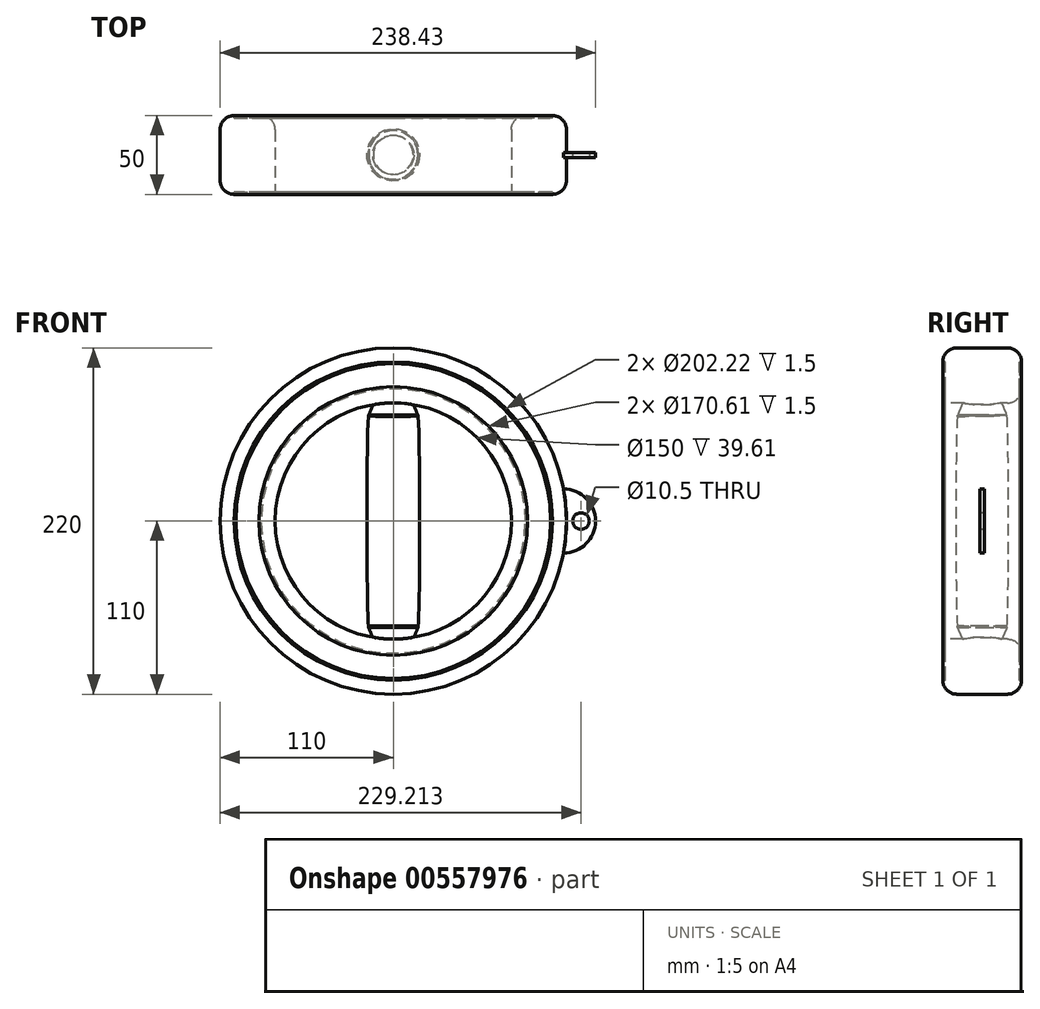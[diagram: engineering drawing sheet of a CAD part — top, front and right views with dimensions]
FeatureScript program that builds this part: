
annotation { "Feature Type Name" : "Feature", "Feature Type Description" : "" }
export const myFeature = defineFeature(function(context is Context, id is Id, definition is map)
    precondition{}
    {
        {
            var Q0;
            Q0=qCreatedBy(makeId("Front.planeOp"),FACE);
            var sketch = newSketch(context, id + "F0", { "sketchPlane" : qUnion([Q0])});
            skCircle(sketch, "E0", {"center": v(0, 0) * mm, "radius": 110 * mm});
            skSolve(sketch);
        }
        {
            var Q0;
            Q0 = qSketchRegion(id + "F0", true);
            extrude(context, id + "F1", {"entities" : qUnion([Q0]), "depth" : 50 * mm, "offsetDistance" : 25.4 * mm});
        }
        {
            var Q0;
            Q0=makeQuery(id+"F1.opExtrude","CAP_FACE",FACE,{"disambiguationData":[OSD([sQuery(id+"F0.wireOp",EDGE,"E0")])],"isStart":false});
            var sketch = newSketch(context, id + "F2", { "sketchPlane" : qUnion([Q0])});
            skCircle(sketch, "E1", {"center": v(0, 0) * mm, "radius": 75 * mm});
            skSolve(sketch);
        }
        {
            var Q0;
            Q0 = qSketchRegion(id + "F2", true);
            extrude(context, id + "F3", {"entities" : qUnion([Q0]), "operationType" : NewBodyOperationType.REMOVE, "endBound" : BoundingType.THROUGH_ALL, "oppositeDirection" : true, "depth" : 25.4 * mm, "offsetDistance" : 25.4 * mm});
        }
        {
            var Q0;
            Q0=qCreatedBy(makeId("Top.planeOp"),FACE);
            cPlane(context, id + "F4", {"entities" : qUnion([Q0]), "cplaneType" : CPlaneType.OFFSET, "offset" : 75.18 * mm, "width" : 152.4 * mm, "height" : 152.4 * mm});
        }
        {
            var Q0;
            Q0=makeQuery(id+"F1.opExtrude","CAP_EDGE",EDGE,{"disambiguationData":[OSD([sQuery(id+"F0.wireOp",EDGE,"E0")])],"isStart":false});
            var Q1;
            Q1=makeQuery(id+"F3.boolean.opBoolean","COPY",EDGE,{"derivedFrom":makeQuery(id+"F3.opExtrude","CAP_EDGE",EDGE,{"disambiguationData":[OSD([sQuery(id+"F2.wireOp",EDGE,"E1")])],"isStart":true})});
            var Q2;
            Q2=makeQuery(id+"F1.opExtrude","CAP_EDGE",EDGE,{"disambiguationData":[OSD([sQuery(id+"F0.wireOp",EDGE,"E0")])],"isStart":true});
            var Q3;
            Q3=makeQuery(id+"F3.boolean.opBoolean","INTERSECT",EDGE,{"derivedFrom":[makeQuery(id+"F1.opExtrude","CAP_FACE",FACE,{"disambiguationData":[OSD([sQuery(id+"F0.wireOp",EDGE,"E0")])],"isStart":true}),makeQuery(id+"F3.opExtrude","SWEPT_FACE",FACE,{"disambiguationData":[OSD([sQuery(id+"F2.wireOp",EDGE,"E1")])]})]});
            fillet(context, id + "F5", {"entities" : qUnion([Q0, Q1, Q2, Q3]), "radius" : 8.9 * mm, "tangentPropagation" : true, "allowEdgeOverflow" : false});
        }
        {
            var Q0;
            Q0=qCreatedBy(id+"F4.planeOp",FACE);
            cPlane(context, id + "F6", {"entities" : qUnion([Q0]), "cplaneType" : CPlaneType.OFFSET, "offset" : 151 * mm, "oppositeDirection" : true, "width" : 150 * mm, "height" : 150 * mm});
        }
        {
            var Q0;
            Q0=qCreatedBy(id+"F4.planeOp",FACE);
            var sketch = newSketch(context, id + "F7", { "sketchPlane" : qUnion([Q0])});
            skCircle(sketch, "E2", {"center": v(0, -25) * mm, "radius": 12.25 * mm});
            skSolve(sketch);
        }
        {
            var Q0;
            Q0=qCreatedBy(id+"F6.planeOp",FACE);
            var sketch = newSketch(context, id + "F8", { "sketchPlane" : qUnion([Q0])});
            skCircle(sketch, "E3", {"center": v(0, -25) * mm, "radius": 12.25 * mm});
            skSolve(sketch);
        }
        {
            var Q0;
            Q0=qCreatedBy(id+"F6.planeOp",FACE);
            cPlane(context, id + "F9", {"entities" : qUnion([Q0]), "cplaneType" : CPlaneType.OFFSET, "offset" : 8.3 * mm, "width" : 150 * mm, "height" : 150 * mm});
        }
        {
            var Q0;
            Q0=qCreatedBy(id+"F4.planeOp",FACE);
            cPlane(context, id + "F10", {"entities" : qUnion([Q0]), "cplaneType" : CPlaneType.OFFSET, "offset" : 8.3 * mm, "oppositeDirection" : true, "width" : 150 * mm, "height" : 150 * mm});
        }
        {
            var Q0;
            Q0=qCreatedBy(id+"F9.planeOp",FACE);
            var sketch = newSketch(context, id + "F11", { "sketchPlane" : qUnion([Q0])});
            skCircle(sketch, "E4", {"center": v(0, -25) * mm, "radius": 15.8 * mm});
            skSolve(sketch);
        }
        {
            var Q0;
            Q0=qCreatedBy(id+"F10.planeOp",FACE);
            var sketch = newSketch(context, id + "F12", { "sketchPlane" : qUnion([Q0])});
            skCircle(sketch, "E5", {"center": v(0, -25.03) * mm, "radius": 15.8 * mm});
            skSolve(sketch);
        }
        {
            var Q0;
            Q0=makeQuery(id+"F11.imprint","IMPRINT",FACE,{"disambiguationData":[TD([[makeQuery(id+"F11.imprint","IMPRINT",EDGE,{"derivedFrom":sQuery(id+"F11.wireOp",EDGE,"E4")}),1.0]])]});
            var Q1;
            Q1=makeQuery(id+"F12.imprint","IMPRINT",FACE,{"disambiguationData":[TD([[makeQuery(id+"F12.imprint","IMPRINT",EDGE,{"derivedFrom":sQuery(id+"F12.wireOp",EDGE,"E5")}),1.0]])]});
            loft(context, id + "F13", {"sheetProfilesArray" : [{ "sheetProfileEntities" : qUnion([Q0]) }, { "sheetProfileEntities" : qUnion([Q1]) }]});
        }
        {
            var Q1;
            Q1 = qSketchRegion(id + "F7", true);
            var Q2;
            Q2 = qSketchRegion(id + "F12", true);
            loft(context, id + "F14", {"operationType" : NewBodyOperationType.ADD, "sheetProfilesArray" : [{ "sheetProfileEntities" : qUnion([Q1]) }, { "sheetProfileEntities" : qUnion([Q2]) }]});
        }
        {
            var Q1;
            Q1 = qSketchRegion(id + "F8", true);
            var Q2;
            Q2 = qSketchRegion(id + "F11", true);
            loft(context, id + "F15", {"operationType" : NewBodyOperationType.ADD, "sheetProfilesArray" : [{ "sheetProfileEntities" : qUnion([Q1]) }, { "sheetProfileEntities" : qUnion([Q2]) }]});
        }
        {
            var Q0;
            Q0=qCreatedBy(makeId("Front.planeOp"),FACE);
            cPlane(context, id + "F16", {"entities" : qUnion([Q0]), "cplaneType" : CPlaneType.OFFSET, "offset" : 25 * mm, "width" : 150 * mm, "height" : 150 * mm});
        }
        {
            var Q0;
            Q0=qCreatedBy(id+"F16.planeOp",FACE);
            var sketch = newSketch(context, id + "F17", { "sketchPlane" : qUnion([Q0])});
            skEllipse(sketch, "E6", {"center": v(15.66, 0) * mm, "majorRadius": 67.26 * mm, "minorRadius": 1.08 * mm, "majorAxis": v(0, -1)});
            skSolve(sketch);
        }
        {
            var Q0;
            Q0=qCreatedBy(id+"F16.planeOp",FACE);
            var sketch = newSketch(context, id + "F18", { "sketchPlane" : qUnion([Q0])});
            skLineSegment(sketch, "E7", {"start": v(0, -80.56) * mm, "end": v(0, 79.26) * mm});
            skSolve(sketch);
        }
        {
            var Q0;
            Q0 = qSketchRegion(id + "F17", true);
            var Q1;
            Q1=sQuery(id+"F18.wireOp",EDGE,"E7");
            revolve(context, id + "F19", {"operationType" : NewBodyOperationType.ADD, "entities" : qUnion([Q0]), "axis" : qUnion([Q1]), "revolveType" : RevolveType.FULL, "oppositeDirection" : true});
        }
        {
            var Q0;
            Q0=makeQuery(id+"F1.opExtrude","CAP_FACE",FACE,{"disambiguationData":[OSD([sQuery(id+"F0.wireOp",EDGE,"E0")])],"isStart":false});
            var sketch = newSketch(context, id + "F20", { "sketchPlane" : qUnion([Q0])});
            skCircle(sketch, "E8", {"center": v(0, 0) * mm, "radius": 85.3 * mm});
            skCircle(sketch, "E9", {"center": v(0, 0) * mm, "radius": 99.97 * mm});
            skSolve(sketch);
        }
        {
            var Q0;
            Q0=makeQuery(id+"F20.imprint","IMPRINT",FACE,{"disambiguationData":[TD([[makeQuery(id+"F20.imprint","IMPRINT",EDGE,{"derivedFrom":sQuery(id+"F20.wireOp",EDGE,"E8")}),1.0]])]});
            var Q1;
            Q1=makeQuery(id+"F20.imprint","IMPRINT",FACE,{"disambiguationData":[TD([[makeQuery(id+"F20.imprint","IMPRINT",EDGE,{"derivedFrom":sQuery(id+"F20.wireOp",EDGE,"E9")}),-1.0]])]});
            extrude(context, id + "F21", {"entities" : qUnion([Q0, Q1]), "operationType" : NewBodyOperationType.REMOVE, "oppositeDirection" : true, "depth" : 1.5 * mm, "offsetDistance" : 25 * mm});
        }
        {
            var Q0;
            Q0=makeQuery(id+"F1.opExtrude","CAP_FACE",FACE,{"disambiguationData":[OSD([sQuery(id+"F0.wireOp",EDGE,"E0")])],"isStart":true});
            var sketch = newSketch(context, id + "F22", { "sketchPlane" : qUnion([Q0])});
            skCircle(sketch, "E10", {"center": v(0, 0) * mm, "radius": 85.3 * mm});
            skCircle(sketch, "E11", {"center": v(0, 0) * mm, "radius": 99.97 * mm});
            skSolve(sketch);
        }
        {
            var Q0;
            Q0=makeQuery(id+"F22.imprint","IMPRINT",FACE,{"disambiguationData":[TD([[makeQuery(id+"F22.imprint","IMPRINT",EDGE,{"derivedFrom":sQuery(id+"F22.wireOp",EDGE,"E11")}),-1.0]])]});
            var Q1;
            Q1=makeQuery(id+"F22.imprint","IMPRINT",FACE,{"disambiguationData":[TD([[makeQuery(id+"F22.imprint","IMPRINT",EDGE,{"derivedFrom":sQuery(id+"F22.wireOp",EDGE,"E10")}),1.0]])]});
            extrude(context, id + "F23", {"entities" : qUnion([Q0, Q1]), "operationType" : NewBodyOperationType.REMOVE, "oppositeDirection" : true, "depth" : 1.5 * mm, "offsetDistance" : 25 * mm});
        }
        {
            var Q0;
            Q0=qCreatedBy(id+"F16.planeOp",FACE);
            var sketch = newSketch(context, id + "F24", { "sketchPlane" : qUnion([Q0])});
            skLineSegment(sketch, "E12", {"start": v(0, 0) * mm, "end": v(136.03, 0) * mm});
            skLineSegment(sketch, "E13", {"start": v(108.11, 0) * mm, "end": v(108.11, 20.4) * mm});
            skLineSegment(sketch, "E14", {"start": v(108.11, 0) * mm, "end": v(108.11, -20.4) * mm});
            skArc(sketch, "E15", {"start": v(108.11, -20.4) * mm, "mid": v(128.43, 0) * mm, "end": v(108.11, 20.4) * mm});
            skSolve(sketch);
        }
        {
            var Q0;
            {var subQ0=sQuery(id+"F24.wireOp",EDGE,"E14");Q0=makeQuery(id+"F24.imprint","IMPRINT",FACE,{"disambiguationData":[TD([[makeQuery(id+"F24.imprint","IMPRINT",EDGE,{"derivedFrom":subQ0}),1.0]])]});}
            var Q1;
            {var subQ0=sQuery(id+"F24.wireOp",EDGE,"E13");Q1=makeQuery(id+"F24.imprint","IMPRINT",FACE,{"disambiguationData":[TD([[makeQuery(id+"F24.imprint","IMPRINT",EDGE,{"derivedFrom":subQ0}),-1.0]])]});}
            extrude(context, id + "F25", {"entities" : qUnion([Q0, Q1]), "operationType" : NewBodyOperationType.ADD, "depth" : 1.5 * mm, "offsetDistance" : 25 * mm});
        }
        {
            var Q0;
            Q0=makeQuery(id+"F25.opExtrude","CAP_FACE",FACE,{"disambiguationData":[OSD([sQuery(id+"F24.wireOp",EDGE,"E13"),sQuery(id+"F24.wireOp",EDGE,"E14"),sQuery(id+"F24.wireOp",EDGE,"E15")])],"isStart":true});
            extrude(context, id + "F26", {"entities" : qUnion([Q0]), "operationType" : NewBodyOperationType.ADD, "depth" : 1.5 * mm, "offsetDistance" : 25 * mm});
        }
        {
            var Q0;
            Q0=makeQuery(id+"F25.opExtrude","CAP_FACE",FACE,{"disambiguationData":[OSD([sQuery(id+"F24.wireOp",EDGE,"E13"),sQuery(id+"F24.wireOp",EDGE,"E14"),sQuery(id+"F24.wireOp",EDGE,"E15")])],"isStart":false});
            var sketch = newSketch(context, id + "F27", { "sketchPlane" : qUnion([Q0])});
            skCircle(sketch, "E16", {"center": v(119.21, 0) * mm, "radius": 5.25 * mm});
            skSolve(sketch);
        }
        {
            var Q0;
            Q0=makeQuery(id+"F27.imprint","IMPRINT",FACE,{"disambiguationData":[TD([[makeQuery(id+"F27.imprint","IMPRINT",EDGE,{"derivedFrom":sQuery(id+"F27.wireOp",EDGE,"E16")}),1.0]])]});
            var Q1;
            Q1=sQuery(id+"F27.wireOp",EDGE,"E16");
            extrude(context, id + "F28", {"entities" : qUnion([Q0]), "operationType" : NewBodyOperationType.REMOVE, "surfaceEntities" : qUnion([Q1]), "endBound" : BoundingType.THROUGH_ALL, "oppositeDirection" : true, "depth" : 25 * mm, "offsetDistance" : 25 * mm});
        }
    });
